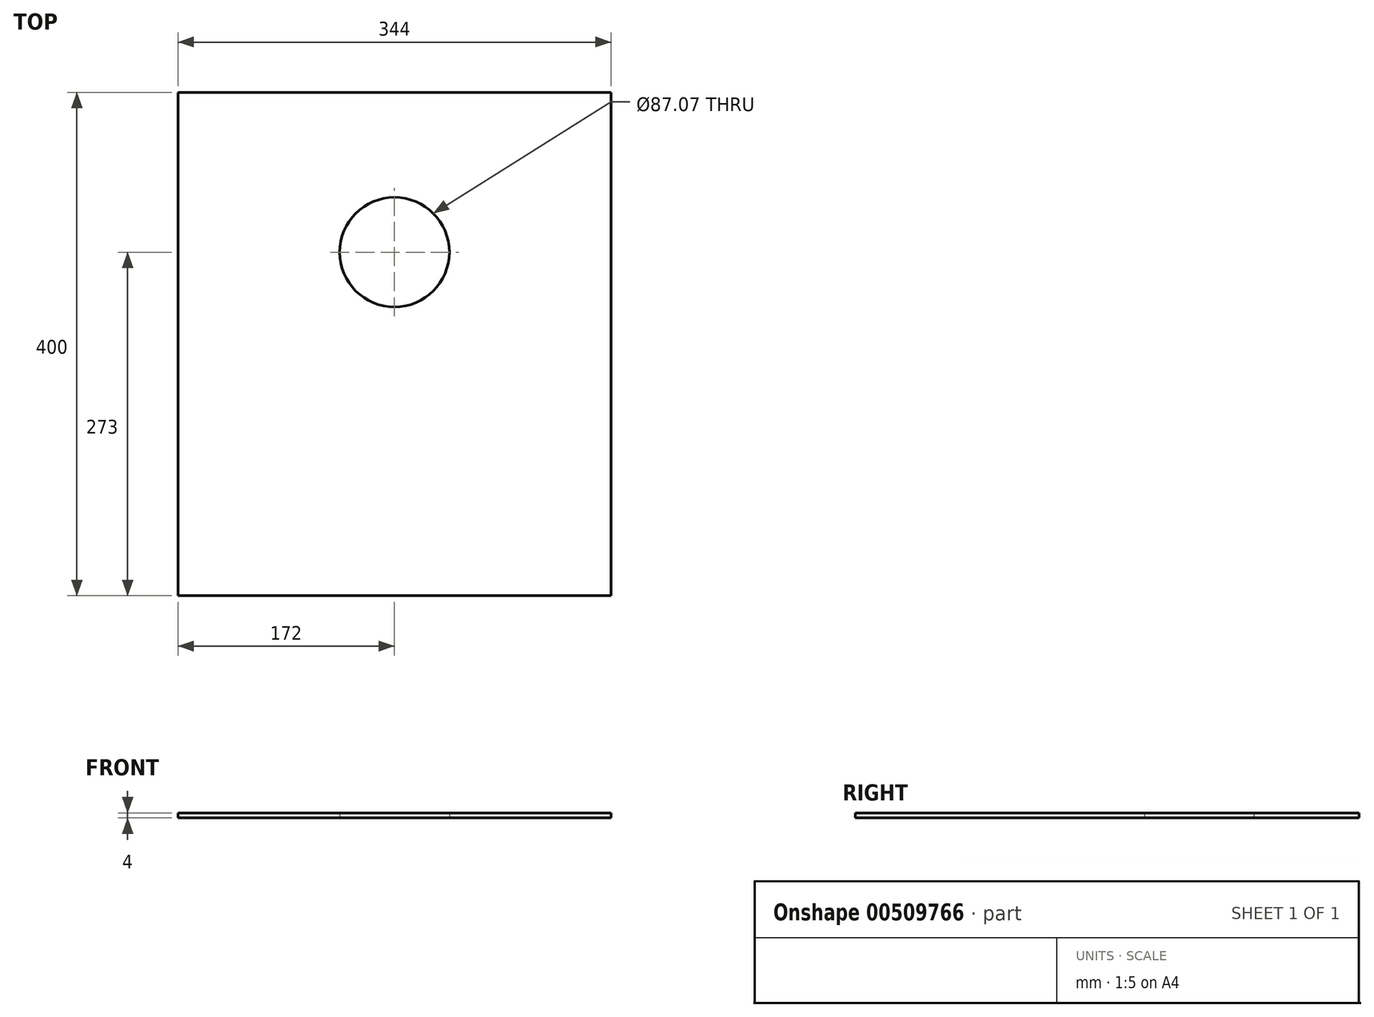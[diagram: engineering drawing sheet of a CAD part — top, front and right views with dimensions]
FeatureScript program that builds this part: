
annotation { "Feature Type Name" : "Feature", "Feature Type Description" : "" }
export const myFeature = defineFeature(function(context is Context, id is Id, definition is map)
    precondition{}
    {
        {
            var Q0;
            Q0=qCreatedBy(makeId("Top.planeOp"),FACE);
            var sketch = newSketch(context, id + "F0", { "sketchPlane" : qUnion([Q0])});
            skLineSegment(sketch, "E0.bottom", {"start": v(0, 0) * mm, "end": v(344, 0) * mm});
            skLineSegment(sketch, "E0.top", {"start": v(0, -400) * mm, "end": v(344, -400) * mm});
            skLineSegment(sketch, "E0.left", {"start": v(0, 0) * mm, "end": v(0, -400) * mm});
            skLineSegment(sketch, "E0.right", {"start": v(344, 0) * mm, "end": v(344, -400) * mm});
            skCircle(sketch, "E1", {"center": v(172, -127) * mm, "radius": 43.54 * mm});
            skSolve(sketch);
        }
        {
            var Q0;
            Q0 = qSketchRegion(id + "F0", true);
            extrude(context, id + "F1", {"entities" : qUnion([Q0]), "depth" : 4 * mm});
        }
    });
